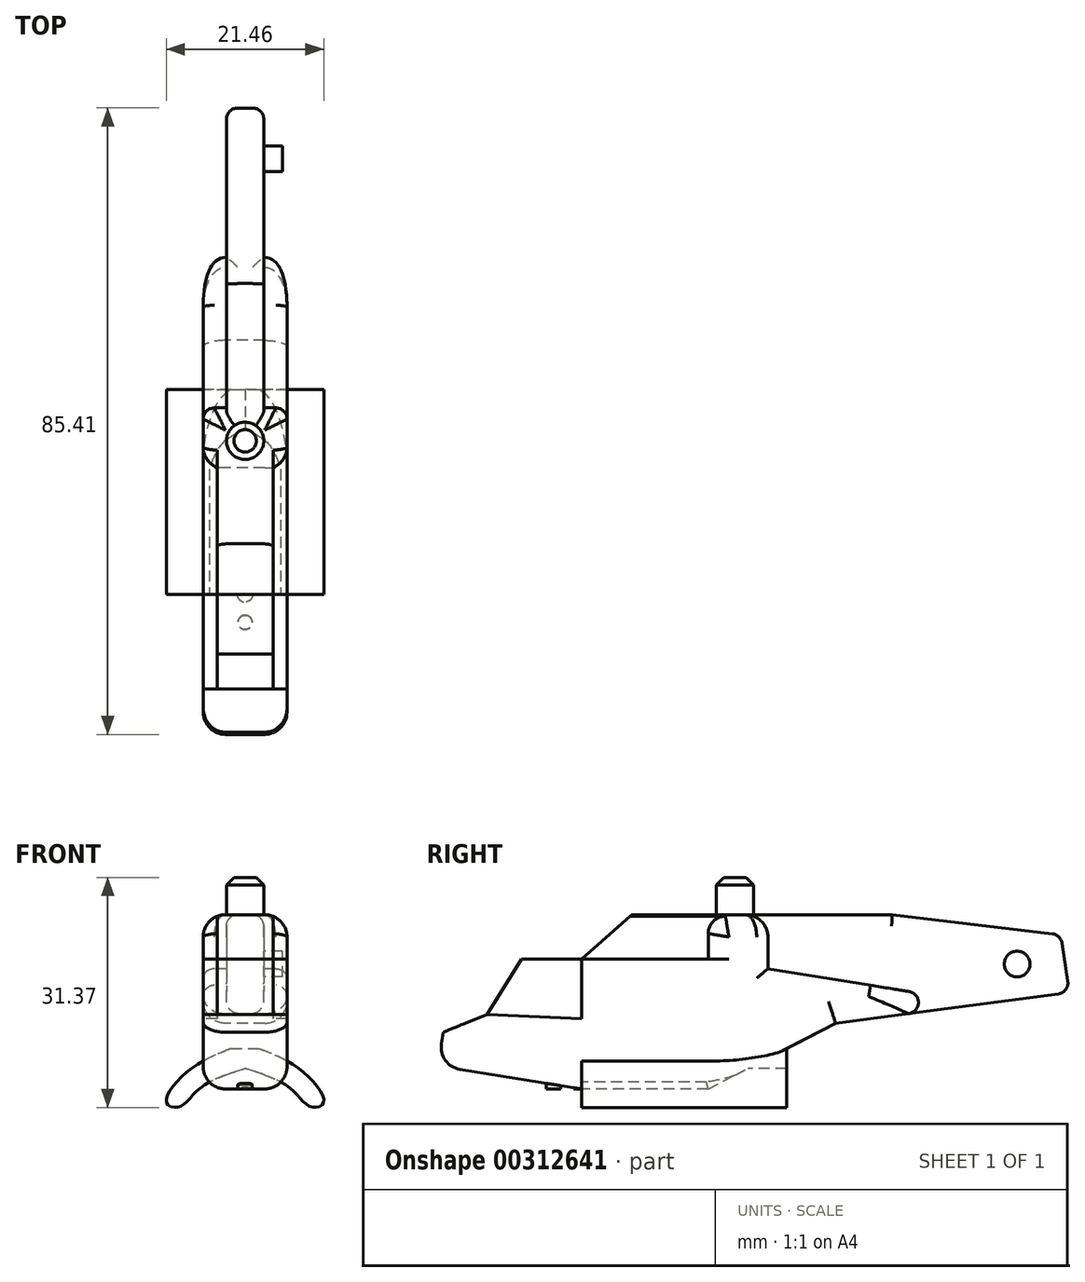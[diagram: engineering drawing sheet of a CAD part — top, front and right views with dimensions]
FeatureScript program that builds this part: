
annotation { "Feature Type Name" : "Feature", "Feature Type Description" : "" }
export const myFeature = defineFeature(function(context is Context, id is Id, definition is map)
    precondition{}
    {
        {
            var Q0;
            Q0=qCreatedBy(makeId("Right.planeOp"),FACE);
            var sketch = newSketch(context, id + "F0", { "sketchPlane" : qUnion([Q0])});
            skLineSegment(sketch, "E0", {"start": v(0, 0) * mm, "end": v(-19.56, 3.15) * mm});
            skLineSegment(sketch, "E1", {"start": v(-19.56, 3.15) * mm, "end": v(-18.82, 7.74) * mm});
            skLineSegment(sketch, "E2", {"start": v(-18.82, 7.74) * mm, "end": v(-12.89, 10.16) * mm});
            skLineSegment(sketch, "E3", {"start": v(-12.89, 10.16) * mm, "end": v(-8.15, 17.7) * mm});
            skLineSegment(sketch, "E4", {"start": v(-8.15, 17.7) * mm, "end": v(0, 17.7) * mm});
            skLineSegment(sketch, "E5", {"start": v(0, 17.7) * mm, "end": v(6.86, 23.77) * mm});
            skLineSegment(sketch, "E6", {"start": v(6.86, 23.77) * mm, "end": v(17.27, 23.77) * mm});
            skLineSegment(sketch, "E7", {"start": v(17.27, 23.77) * mm, "end": v(17.27, 0) * mm});
            skLineSegment(sketch, "E8", {"start": v(17.27, 0) * mm, "end": v(0, 0) * mm});
            skLineSegment(sketch, "E9", {"start": v(17.27, 0) * mm, "end": v(34.62, 8.96) * mm});
            skLineSegment(sketch, "E10", {"start": v(34.62, 8.96) * mm, "end": v(66.51, 13.16) * mm});
            skLineSegment(sketch, "E11", {"start": v(17.27, 23.77) * mm, "end": v(42.36, 23.77) * mm});
            skLineSegment(sketch, "E12", {"start": v(42.36, 23.77) * mm, "end": v(65.31, 21.04) * mm});
            skLineSegment(sketch, "E13", {"start": v(65.31, 21.04) * mm, "end": v(66.51, 13.16) * mm});
            skLineSegment(sketch, "E14", {"start": v(0, 17.7) * mm, "end": v(0, 9.58) * mm});
            skLineSegment(sketch, "E15", {"start": v(0, 9.58) * mm, "end": v(-12.89, 10.16) * mm});
            skLineSegment(sketch, "E16", {"start": v(0, 17.7) * mm, "end": v(17.27, 17.7) * mm});
            skLineSegment(sketch, "E17", {"start": v(17.27, 17.7) * mm, "end": v(34.62, 8.96) * mm});
            skLineSegment(sketch, "E18", {"start": v(17.27, 17.7) * mm, "end": v(54.92, 11.63) * mm});
            skLineSegment(sketch, "E19", {"start": v(38.8, 14.23) * mm, "end": v(66.51, 13.16) * mm});
            skLineSegment(sketch, "E20", {"start": v(25.4, 23.77) * mm, "end": v(25.4, 16.39) * mm});
            skSolve(sketch);
        }
        {
            var Q0;
            Q0=makeQuery(id+"F0.imprint","IMPRINT",FACE,{"disambiguationData":[TD([[makeQuery(id+"F0.imprint","IMPRINT",EDGE,{"derivedFrom":sQuery(id+"F0.wireOp",EDGE,"E0")}),-1.0]])]});
            extrude(context, id + "F1", {"entities" : qUnion([Q0]), "depth" : 5.7 * mm});
        }
        {
            var Q0;
            Q0=makeQuery(id+"F0.imprint","IMPRINT",FACE,{"disambiguationData":[TD([[makeQuery(id+"F0.imprint","IMPRINT",EDGE,{"derivedFrom":sQuery(id+"F0.wireOp",EDGE,"E0")}),-1.0]])]});
            extrude(context, id + "F2", {"entities" : qUnion([Q0]), "operationType" : NewBodyOperationType.ADD, "oppositeDirection" : true, "depth" : 5.7 * mm});
        }
        {
            var Q0;
            Q0=makeQuery(id+"F0.imprint","IMPRINT",FACE,{"disambiguationData":[TD([[makeQuery(id+"F0.imprint","IMPRINT",EDGE,{"derivedFrom":sQuery(id+"F0.wireOp",EDGE,"E3")}),-1.0]])]});
            extrude(context, id + "F3", {"entities" : qUnion([Q0]), "operationType" : NewBodyOperationType.ADD, "depth" : 3.8 * mm});
        }
        {
            var Q0;
            Q0=makeQuery(id+"F0.imprint","IMPRINT",FACE,{"disambiguationData":[TD([[makeQuery(id+"F0.imprint","IMPRINT",EDGE,{"derivedFrom":sQuery(id+"F0.wireOp",EDGE,"E5")}),-1.0]])]});
            extrude(context, id + "F4", {"entities" : qUnion([Q0]), "operationType" : NewBodyOperationType.ADD, "depth" : 3.8 * mm});
        }
        {
            var Q0;
            Q0=makeQuery(id+"F0.imprint","IMPRINT",FACE,{"disambiguationData":[TD([[makeQuery(id+"F0.imprint","IMPRINT",EDGE,{"derivedFrom":sQuery(id+"F0.wireOp",EDGE,"E3")}),-1.0]])]});
            extrude(context, id + "F5", {"entities" : qUnion([Q0]), "operationType" : NewBodyOperationType.ADD, "oppositeDirection" : true, "depth" : 3.8 * mm});
        }
        {
            var Q0;
            Q0=makeQuery(id+"F0.imprint","IMPRINT",FACE,{"disambiguationData":[TD([[makeQuery(id+"F0.imprint","IMPRINT",EDGE,{"derivedFrom":sQuery(id+"F0.wireOp",EDGE,"E5")}),-1.0]])]});
            extrude(context, id + "F6", {"entities" : qUnion([Q0]), "operationType" : NewBodyOperationType.ADD, "oppositeDirection" : true, "depth" : 3.8 * mm});
        }
        {
            var Q0;
            {var subQ0=sQuery(id+"F0.wireOp",EDGE,"E9");Q0=makeQuery(id+"F0.imprint","IMPRINT",FACE,{"disambiguationData":[TD([[makeQuery(id+"F0.imprint","IMPRINT",EDGE,{"derivedFrom":subQ0}),1.0]])]});}
            var Q1;
            {var subQ0=sQuery(id+"F0.wireOp",EDGE,"E17");Q1=makeQuery(id+"F0.imprint","IMPRINT",FACE,{"disambiguationData":[TD([[makeQuery(id+"F0.imprint","IMPRINT",EDGE,{"derivedFrom":subQ0}),1.0]])]});}
            extrude(context, id + "F7", {"entities" : qUnion([Q0, Q1]), "operationType" : NewBodyOperationType.ADD, "depth" : 5.7 * mm});
        }
        {
            var Q0;
            {var subQ0=sQuery(id+"F0.wireOp",EDGE,"E17");Q0=makeQuery(id+"F0.imprint","IMPRINT",FACE,{"disambiguationData":[TD([[makeQuery(id+"F0.imprint","IMPRINT",EDGE,{"derivedFrom":subQ0}),1.0]])]});}
            var Q1;
            {var subQ0=sQuery(id+"F0.wireOp",EDGE,"E9");Q1=makeQuery(id+"F0.imprint","IMPRINT",FACE,{"disambiguationData":[TD([[makeQuery(id+"F0.imprint","IMPRINT",EDGE,{"derivedFrom":subQ0}),1.0]])]});}
            extrude(context, id + "F8", {"entities" : qUnion([Q0, Q1]), "operationType" : NewBodyOperationType.ADD, "oppositeDirection" : true, "depth" : 5.7 * mm});
        }
        {
            var Q0;
            {var subQ5=sQuery(id+"F0.wireOp",EDGE,"E20");Q0=makeQuery(id+"F0.imprint","IMPRINT",FACE,{"disambiguationData":[TD([[makeQuery(id+"F0.imprint","IMPRINT",EDGE,{"derivedFrom":subQ5}),-1.0]])]});}
            extrude(context, id + "F9", {"entities" : qUnion([Q0]), "operationType" : NewBodyOperationType.ADD, "depth" : 5.7 * mm});
        }
        {
            var Q0;
            {var subQ5=sQuery(id+"F0.wireOp",EDGE,"E20");Q0=makeQuery(id+"F0.imprint","IMPRINT",FACE,{"disambiguationData":[TD([[makeQuery(id+"F0.imprint","IMPRINT",EDGE,{"derivedFrom":subQ5}),-1.0]])]});}
            extrude(context, id + "F10", {"entities" : qUnion([Q0]), "operationType" : NewBodyOperationType.ADD, "oppositeDirection" : true, "depth" : 5.7 * mm});
        }
        {
            var Q0;
            {var subQ3=sQuery(id+"F0.wireOp",EDGE,"E12");Q0=makeQuery(id+"F0.imprint","IMPRINT",FACE,{"disambiguationData":[TD([[makeQuery(id+"F0.imprint","IMPRINT",EDGE,{"derivedFrom":subQ3}),-1.0]])]});}
            var Q1;
            {var subQ0=sQuery(id+"F0.wireOp",EDGE,"E19");Q1=makeQuery(id+"F0.imprint","IMPRINT",FACE,{"disambiguationData":[TD([[makeQuery(id+"F0.imprint","IMPRINT",EDGE,{"derivedFrom":subQ0}),-1.0]])]});}
            extrude(context, id + "F11", {"entities" : qUnion([Q0, Q1]), "operationType" : NewBodyOperationType.ADD, "depth" : 2.54 * mm});
        }
        {
            var Q0;
            {var subQ3=sQuery(id+"F0.wireOp",EDGE,"E12");Q0=makeQuery(id+"F0.imprint","IMPRINT",FACE,{"disambiguationData":[TD([[makeQuery(id+"F0.imprint","IMPRINT",EDGE,{"derivedFrom":subQ3}),-1.0]])]});}
            var Q1;
            {var subQ0=sQuery(id+"F0.wireOp",EDGE,"E19");Q1=makeQuery(id+"F0.imprint","IMPRINT",FACE,{"disambiguationData":[TD([[makeQuery(id+"F0.imprint","IMPRINT",EDGE,{"derivedFrom":subQ0}),-1.0]])]});}
            extrude(context, id + "F12", {"entities" : qUnion([Q0, Q1]), "operationType" : NewBodyOperationType.ADD, "oppositeDirection" : true, "depth" : 2.54 * mm});
        }
        {
            var Q0;
            Q0=makeQuery(id+"F11.opExtrude","CAP_EDGE",EDGE,{"disambiguationData":[OSD([sQuery(id+"F0.wireOp",EDGE,"E13")])],"isStart":false});
            var Q1;
            {var subQ0=sQuery(id+"F0.wireOp",EDGE,"E13");var subQ1=sQuery(id+"F0.wireOp",EDGE,"E12");Q1=makeQuery(id+"F12.boolean.opBoolean","MERGE",EDGE,{"derivedFrom":[makeQuery(id+"F11.opExtrude","SWEPT_EDGE",EDGE,{"disambiguationData":[OSD([subQ1,subQ0])]}),makeQuery(id+"F12.opExtrude","SWEPT_EDGE",EDGE,{"disambiguationData":[OSD([subQ1,subQ0])]})]});}
            var Q2;
            Q2=makeQuery(id+"F12.opExtrude","CAP_EDGE",EDGE,{"disambiguationData":[OSD([sQuery(id+"F0.wireOp",EDGE,"E13")])],"isStart":false});
            var Q3;
            {var subQ0=sQuery(id+"F0.wireOp",EDGE,"E19");var subQ1=sQuery(id+"F0.wireOp",EDGE,"E13");var subQ2=sQuery(id+"F0.wireOp",EDGE,"E10");Q3=makeQuery(id+"F12.boolean.opBoolean","MERGE",EDGE,{"derivedFrom":[makeQuery(id+"F11.opExtrude","SWEPT_EDGE",EDGE,{"disambiguationData":[OSD([subQ2,subQ1,subQ0])]}),makeQuery(id+"F12.opExtrude","SWEPT_EDGE",EDGE,{"disambiguationData":[OSD([subQ2,subQ1,subQ0])]})]});}
            var Q4;
            Q4=makeQuery(id+"F11.opExtrude","CAP_EDGE",EDGE,{"disambiguationData":[OSD([sQuery(id+"F0.wireOp",EDGE,"E12")])],"isStart":false});
            var Q5;
            Q5=makeQuery(id+"F12.opExtrude","CAP_EDGE",EDGE,{"disambiguationData":[OSD([sQuery(id+"F0.wireOp",EDGE,"E12")])],"isStart":false});
            var Q6;
            Q6=makeQuery(id+"F12.opExtrude","CAP_EDGE",EDGE,{"disambiguationData":[OSD([sQuery(id+"F0.wireOp",EDGE,"E10")])],"isStart":false});
            var Q7;
            Q7=makeQuery(id+"F11.opExtrude","CAP_EDGE",EDGE,{"disambiguationData":[OSD([sQuery(id+"F0.wireOp",EDGE,"E10")])],"isStart":false});
            var Q8;
            Q8=makeQuery(id+"F7.opExtrude","CAP_EDGE",EDGE,{"disambiguationData":[OSD([sQuery(id+"F0.wireOp",EDGE,"E18")])],"isStart":false});
            var Q9;
            Q9=makeQuery(id+"F8.opExtrude","CAP_EDGE",EDGE,{"disambiguationData":[OSD([sQuery(id+"F0.wireOp",EDGE,"E18")])],"isStart":false});
            var Q10;
            Q10=makeQuery(id+"F9.opExtrude","CAP_EDGE",EDGE,{"disambiguationData":[OSD([sQuery(id+"F0.wireOp",EDGE,"E20")])],"isStart":false});
            var Q11;
            {var subQ0=sQuery(id+"F0.wireOp",EDGE,"E18");var subQ1=sQuery(id+"F0.wireOp",EDGE,"E10");var subQ2=sQuery(id+"F0.wireOp",EDGE,"E7");var subQ3=sQuery(id+"F0.wireOp",EDGE,"E20");Q11=makeQuery(id+"F11.boolean.opBoolean","SPLIT",EDGE,{"disambiguationData":[TD([makeQuery(id+"F7.opExtrude","CAP_FACE",FACE,{"disambiguationData":[OSD([subQ2,sQuery(id+"F0.wireOp",EDGE,"E9"),subQ1,subQ0])],"isStart":false})])],"derivedFrom":makeQuery(id+"F10.boolean.opBoolean","MERGE",EDGE,{"derivedFrom":[makeQuery(id+"F9.opExtrude","SWEPT_EDGE",EDGE,{"disambiguationData":[OSD([subQ0,subQ3])]}),makeQuery(id+"F10.opExtrude","SWEPT_EDGE",EDGE,{"disambiguationData":[OSD([subQ0,subQ3])]})]})});}
            var Q12;
            Q12=makeQuery(id+"F10.opExtrude","CAP_EDGE",EDGE,{"disambiguationData":[OSD([sQuery(id+"F0.wireOp",EDGE,"E20")])],"isStart":false});
            var Q13;
            {var subQ0=sQuery(id+"F0.wireOp",EDGE,"E18");var subQ1=sQuery(id+"F0.wireOp",EDGE,"E10");var subQ2=sQuery(id+"F0.wireOp",EDGE,"E7");var subQ3=sQuery(id+"F0.wireOp",EDGE,"E20");Q13=makeQuery(id+"F11.boolean.opBoolean","SPLIT",EDGE,{"disambiguationData":[TD([makeQuery(id+"F8.opExtrude","CAP_FACE",FACE,{"disambiguationData":[OSD([subQ2,sQuery(id+"F0.wireOp",EDGE,"E9"),subQ1,subQ0])],"isStart":false})])],"derivedFrom":makeQuery(id+"F10.boolean.opBoolean","MERGE",EDGE,{"derivedFrom":[makeQuery(id+"F9.opExtrude","SWEPT_EDGE",EDGE,{"disambiguationData":[OSD([subQ0,subQ3])]}),makeQuery(id+"F10.opExtrude","SWEPT_EDGE",EDGE,{"disambiguationData":[OSD([subQ0,subQ3])]})]})});}
            var Q14;
            {var subQ0=sQuery(id+"F0.wireOp",EDGE,"E18");var subQ1=sQuery(id+"F0.wireOp",EDGE,"E10");var subQ2=sQuery(id+"F0.wireOp",EDGE,"E7");Q14=makeQuery(id+"F11.boolean.opBoolean","SPLIT",EDGE,{"disambiguationData":[TD([makeQuery(id+"F7.opExtrude","CAP_FACE",FACE,{"disambiguationData":[OSD([subQ2,sQuery(id+"F0.wireOp",EDGE,"E9"),subQ1,subQ0])],"isStart":false})])],"derivedFrom":makeQuery(id+"F8.boolean.opBoolean","MERGE",EDGE,{"derivedFrom":[makeQuery(id+"F7.opExtrude","SWEPT_EDGE",EDGE,{"disambiguationData":[OSD([subQ1,subQ0])]}),makeQuery(id+"F8.opExtrude","SWEPT_EDGE",EDGE,{"disambiguationData":[OSD([subQ1,subQ0])]})]})});}
            var Q15;
            {var subQ0=sQuery(id+"F0.wireOp",EDGE,"E18");var subQ1=sQuery(id+"F0.wireOp",EDGE,"E10");var subQ2=sQuery(id+"F0.wireOp",EDGE,"E7");Q15=makeQuery(id+"F11.boolean.opBoolean","SPLIT",EDGE,{"disambiguationData":[TD([makeQuery(id+"F8.opExtrude","CAP_FACE",FACE,{"disambiguationData":[OSD([subQ2,sQuery(id+"F0.wireOp",EDGE,"E9"),subQ1,subQ0])],"isStart":false})])],"derivedFrom":makeQuery(id+"F8.boolean.opBoolean","MERGE",EDGE,{"derivedFrom":[makeQuery(id+"F7.opExtrude","SWEPT_EDGE",EDGE,{"disambiguationData":[OSD([subQ1,subQ0])]}),makeQuery(id+"F8.opExtrude","SWEPT_EDGE",EDGE,{"disambiguationData":[OSD([subQ1,subQ0])]})]})});}
            var Q16;
            Q16=makeQuery(id+"F12.opExtrude","CAP_EDGE",EDGE,{"disambiguationData":[OSD([sQuery(id+"F0.wireOp",EDGE,"E11")])],"isStart":false});
            var Q17;
            Q17=makeQuery(id+"F11.opExtrude","CAP_EDGE",EDGE,{"disambiguationData":[OSD([sQuery(id+"F0.wireOp",EDGE,"E11")])],"isStart":false});
            fillet(context, id + "F13", {"entities" : qUnion([Q0, Q1, Q2, Q3, Q4, Q5, Q6, Q7, Q8, Q9, Q10, Q11, Q12, Q13, Q14, Q15, Q16, Q17]), "radius" : 1.52 * mm, "tangentPropagation" : true, "allowEdgeOverflow" : false});
        }
        {
            var Q0;
            Q0=makeQuery(id+"F11.opExtrude","CAP_FACE",FACE,{"disambiguationData":[OSD([sQuery(id+"F0.wireOp",EDGE,"E10"),sQuery(id+"F0.wireOp",EDGE,"E11"),sQuery(id+"F0.wireOp",EDGE,"E12"),sQuery(id+"F0.wireOp",EDGE,"E13"),sQuery(id+"F0.wireOp",EDGE,"E18"),sQuery(id+"F0.wireOp",EDGE,"E20")])],"isStart":false});
            var sketch = newSketch(context, id + "F14", { "sketchPlane" : qUnion([Q0])});
            skCircle(sketch, "E21", {"center": v(59.37, 17.03) * mm, "radius": 1.75 * mm});
            skSolve(sketch);
        }
        {
            var Q0;
            Q0=makeQuery(id+"F14.imprint","IMPRINT",FACE,{"disambiguationData":[TD([[makeQuery(id+"F14.imprint","IMPRINT",EDGE,{"derivedFrom":sQuery(id+"F14.wireOp",EDGE,"E21")}),1.0]])]});
            extrude(context, id + "F15", {"entities" : qUnion([Q0]), "operationType" : NewBodyOperationType.ADD, "depth" : 2.54 * mm});
        }
        {
            var Q0;
            {var subQ0=sQuery(id+"F0.wireOp",EDGE,"E11");var subQ1=sQuery(id+"F0.wireOp",EDGE,"E6");Q0=makeQuery(id+"F12.boolean.opBoolean","MERGE",FACE,{"derivedFrom":[makeQuery(id+"F11.boolean.opBoolean","MERGE",FACE,{"derivedFrom":[makeQuery(id+"F10.boolean.opBoolean","MERGE",FACE,{"derivedFrom":[makeQuery(id+"F9.boolean.opBoolean","MERGE",FACE,{"derivedFrom":[makeQuery(id+"F6.boolean.opBoolean","MERGE",FACE,{"derivedFrom":[makeQuery(id+"F4.opExtrude","SWEPT_FACE",FACE,{"disambiguationData":[OSD([subQ1])]}),makeQuery(id+"F6.opExtrude","SWEPT_FACE",FACE,{"disambiguationData":[OSD([subQ1])]})]}),makeQuery(id+"F9.opExtrude","SWEPT_FACE",FACE,{"disambiguationData":[OSD([subQ0])]})]}),makeQuery(id+"F10.opExtrude","SWEPT_FACE",FACE,{"disambiguationData":[OSD([subQ0])]})]}),makeQuery(id+"F11.opExtrude","SWEPT_FACE",FACE,{"disambiguationData":[OSD([subQ0])]})]}),makeQuery(id+"F12.opExtrude","SWEPT_FACE",FACE,{"disambiguationData":[OSD([subQ0])]})]});}
            var sketch = newSketch(context, id + "F16", { "sketchPlane" : qUnion([Q0])});
            skCircle(sketch, "E22", {"center": v(0, 20.92) * mm, "radius": 2.54 * mm});
            skSolve(sketch);
        }
        {
            var Q0;
            Q0=makeQuery(id+"F16.imprint","IMPRINT",FACE,{"disambiguationData":[TD([[makeQuery(id+"F16.imprint","IMPRINT",EDGE,{"derivedFrom":sQuery(id+"F16.wireOp",EDGE,"E22")}),1.0]])]});
            extrude(context, id + "F17", {"entities" : qUnion([Q0]), "operationType" : NewBodyOperationType.ADD, "depth" : 5.08 * mm});
        }
        {
            var Q0;
            Q0=makeQuery(id+"F10.opExtrude","CAP_EDGE",EDGE,{"disambiguationData":[OSD([sQuery(id+"F0.wireOp",EDGE,"E11")])],"isStart":false});
            var Q1;
            Q1=makeQuery(id+"F9.opExtrude","CAP_EDGE",EDGE,{"disambiguationData":[OSD([sQuery(id+"F0.wireOp",EDGE,"E11")])],"isStart":false});
            var Q2;
            Q2=makeQuery(id+"F10.opExtrude","CAP_EDGE",EDGE,{"disambiguationData":[OSD([sQuery(id+"F0.wireOp",EDGE,"E7")])],"isStart":false});
            var Q3;
            Q3=makeQuery(id+"F9.opExtrude","CAP_EDGE",EDGE,{"disambiguationData":[OSD([sQuery(id+"F0.wireOp",EDGE,"E7")])],"isStart":false});
            fillet(context, id + "F18", {"entities" : qUnion([Q0, Q1, Q2, Q3]), "radius" : 3.05 * mm, "tangentPropagation" : true, "allowEdgeOverflow" : false});
        }
        {
            var Q0;
            Q0=makeQuery(id+"F17.opExtrude","CAP_EDGE",EDGE,{"disambiguationData":[OSD([sQuery(id+"F16.wireOp",EDGE,"E22")])],"isStart":false});
            chamfer(context, id + "F19", {"entities" : qUnion([Q0]), "width" : 1.02 * mm});
        }
        {
            var Q0;
            Q0=makeQuery(id+"F8.opExtrude","CAP_EDGE",EDGE,{"disambiguationData":[OSD([sQuery(id+"F0.wireOp",EDGE,"E9")])],"isStart":false});
            var Q1;
            Q1=makeQuery(id+"F8.opExtrude","CAP_EDGE",EDGE,{"disambiguationData":[OSD([sQuery(id+"F0.wireOp",EDGE,"E10")])],"isStart":false});
            var Q2;
            Q2=makeQuery(id+"F7.opExtrude","CAP_EDGE",EDGE,{"disambiguationData":[OSD([sQuery(id+"F0.wireOp",EDGE,"E10")])],"isStart":false});
            var Q3;
            Q3=makeQuery(id+"F7.opExtrude","CAP_EDGE",EDGE,{"disambiguationData":[OSD([sQuery(id+"F0.wireOp",EDGE,"E9")])],"isStart":false});
            var Q4;
            Q4=makeQuery(id+"F2.opExtrude","CAP_EDGE",EDGE,{"disambiguationData":[OSD([sQuery(id+"F0.wireOp",EDGE,"E8")])],"isStart":false});
            var Q5;
            Q5=makeQuery(id+"F1.opExtrude","CAP_EDGE",EDGE,{"disambiguationData":[OSD([sQuery(id+"F0.wireOp",EDGE,"E8")])],"isStart":false});
            var Q6;
            Q6=makeQuery(id+"F2.opExtrude","CAP_EDGE",EDGE,{"disambiguationData":[OSD([sQuery(id+"F0.wireOp",EDGE,"E0")])],"isStart":false});
            var Q7;
            Q7=makeQuery(id+"F1.opExtrude","CAP_EDGE",EDGE,{"disambiguationData":[OSD([sQuery(id+"F0.wireOp",EDGE,"E0")])],"isStart":false});
            var Q8;
            Q8=makeQuery(id+"F2.opExtrude","CAP_EDGE",EDGE,{"disambiguationData":[OSD([sQuery(id+"F0.wireOp",EDGE,"E1")])],"isStart":false});
            var Q9;
            Q9=makeQuery(id+"F1.opExtrude","CAP_EDGE",EDGE,{"disambiguationData":[OSD([sQuery(id+"F0.wireOp",EDGE,"E1")])],"isStart":false});
            var Q10;
            {var subQ0=sQuery(id+"F0.wireOp",EDGE,"E1");var subQ1=sQuery(id+"F0.wireOp",EDGE,"E0");Q10=makeQuery(id+"F2.boolean.opBoolean","MERGE",EDGE,{"derivedFrom":[makeQuery(id+"F1.opExtrude","SWEPT_EDGE",EDGE,{"disambiguationData":[OSD([subQ1,subQ0])]}),makeQuery(id+"F2.opExtrude","SWEPT_EDGE",EDGE,{"disambiguationData":[OSD([subQ1,subQ0])]})]});}
            fillet(context, id + "F20", {"entities" : qUnion([Q0, Q1, Q2, Q3, Q4, Q5, Q6, Q7, Q8, Q9, Q10]), "radius" : 3.05 * mm, "tangentPropagation" : true, "allowEdgeOverflow" : false});
        }
        {
            var Q0;
            Q0=makeQuery(id+"F18.opFillet","BLEND_EDGE",EDGE,{"blendedFrom":[makeQuery(id+"F10.opExtrude","CAP_EDGE",EDGE,{"disambiguationData":[OSD([sQuery(id+"F0.wireOp",EDGE,"E7")])],"isStart":false}),makeQuery(id+"F10.opExtrude","CAP_EDGE",EDGE,{"disambiguationData":[OSD([sQuery(id+"F0.wireOp",EDGE,"E11")])],"isStart":false})],"blendedInto":[]});
            var Q1;
            Q1=makeQuery(id+"F18.opFillet","BLEND_EDGE",EDGE,{"blendedFrom":[makeQuery(id+"F9.opExtrude","CAP_EDGE",EDGE,{"disambiguationData":[OSD([sQuery(id+"F0.wireOp",EDGE,"E7")])],"isStart":false}),makeQuery(id+"F9.opExtrude","CAP_EDGE",EDGE,{"disambiguationData":[OSD([sQuery(id+"F0.wireOp",EDGE,"E11")])],"isStart":false})],"blendedInto":[]});
            fillet(context, id + "F21", {"entities" : qUnion([Q0, Q1]), "radius" : 2.54 * mm, "tangentPropagation" : true, "allowEdgeOverflow" : false});
        }
        {
            var Q0;
            Q0=qCreatedBy(makeId("Front.planeOp"),FACE);
            var sketch = newSketch(context, id + "F22", { "sketchPlane" : qUnion([Q0])});
            skFitSpline(sketch, "E23", {"points": [v(0, 6.2) * mm, v(7.76, 2.44) * mm, v(10.69, -1.86) * mm, v(8.97, -2.44) * mm, v(6.28, 0) * mm, v(0, 2.8) * mm], "startDerivative": vector(31.05, -11) * mm, "endDerivative": vector(-30.27, 9.7) * mm});
            skLineSegment(sketch, "E24", {"start": v(0, 20.69) * mm, "end": v(0, -4.12) * mm});
            skFitSpline(sketch, "E25.MirrorCS", {"points": [v(0, 6.2) * mm, v(-7.76, 2.44) * mm, v(-10.69, -1.86) * mm, v(-8.97, -2.44) * mm, v(-6.28, 0) * mm, v(0, 2.8) * mm], "startDerivative": vector(-31.05, -11) * mm, "endDerivative": vector(30.27, 9.7) * mm});
            skSolve(sketch);
        }
        {
            var Q0;
            {var subQ0=sQuery(id+"F22.wireOp",EDGE,"E25.MirrorCS");Q0=makeQuery(id+"F22.imprint","IMPRINT",FACE,{"disambiguationData":[TD([[makeQuery(id+"F22.imprint","IMPRINT",EDGE,{"derivedFrom":subQ0}),1.0]])]});}
            var Q1;
            {var subQ0=sQuery(id+"F22.wireOp",EDGE,"E23");Q1=makeQuery(id+"F22.imprint","IMPRINT",FACE,{"disambiguationData":[TD([[makeQuery(id+"F22.imprint","IMPRINT",EDGE,{"derivedFrom":subQ0}),-1.0]])]});}
            extrude(context, id + "F23", {"entities" : qUnion([Q0, Q1]), "operationType" : NewBodyOperationType.ADD, "oppositeDirection" : true, "depth" : 27.94 * mm});
        }
        {
            var Q0;
            Q0=qCreatedBy(makeId("Top.planeOp"),FACE);
            var sketch = newSketch(context, id + "F24", { "sketchPlane" : qUnion([Q0])});
            skCircle(sketch, "E26", {"center": v(0, 0) * mm, "radius": 1.07 * mm});
            skCircle(sketch, "E27", {"center": v(0, -3.84) * mm, "radius": 0.98 * mm});
            skSolve(sketch);
        }
        {
            var Q0;
            Q0=makeQuery(id+"F24.imprint","IMPRINT",FACE,{"disambiguationData":[TD([[makeQuery(id+"F24.imprint","IMPRINT",EDGE,{"derivedFrom":sQuery(id+"F24.wireOp",EDGE,"E27")}),1.0]])]});
            var Q1;
            Q1=makeQuery(id+"F24.imprint","IMPRINT",FACE,{"disambiguationData":[TD([[makeQuery(id+"F24.imprint","IMPRINT",EDGE,{"derivedFrom":sQuery(id+"F24.wireOp",EDGE,"E26")}),1.0]])]});
            extrude(context, id + "F25", {"entities" : qUnion([Q0, Q1]), "operationType" : NewBodyOperationType.ADD, "depth" : 12.7 * mm});
        }
    });
